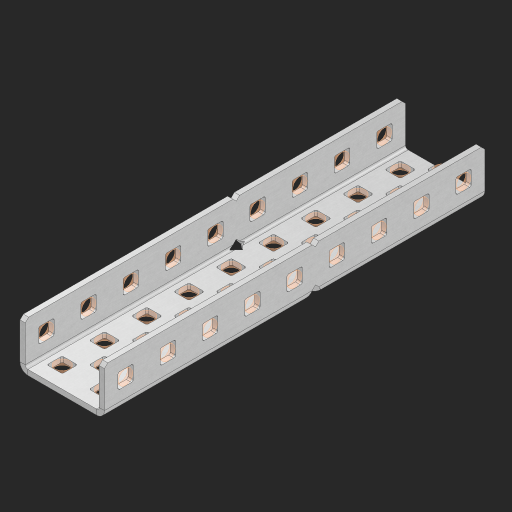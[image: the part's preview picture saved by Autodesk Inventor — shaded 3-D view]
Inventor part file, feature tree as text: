
AUTODESK INVENTOR PART (.ipt)
format: ipt  version: 2023 (Build 270158000, 158)  size: 888,320 bytes
history: native  units: in
note: dims shown in document units (in); Inventor stores cm internally (conversion verified against a paired STEP export)
features: other x52, extrude x43, sheet_metal_op x11, sketch x10, pattern_linear x2, mirror x1, chamfer x1
ambient origin geometry x8: Origin, YZ Plane, XZ Plane, XY Plane, X Axis, Y Axis, Z Axis, Center Point
bodies: Solid1 (feature_tree), Body (feature_tree)
feature tree (120):
  sheet_metal_op  "Flanges"
  other  "Flange Pattern Plane"
  other  "Flange Pattern Sketch"
  sheet_metal_op  "Flange Pattern"
  sheet_metal_op  "Body Pattern"
  pattern_linear  "Center Pattern"  Spacing1=0.0625in  [1 undecoded]
  other  "Arc Length"
  mirror  "Notch Mirror"
  pattern_linear  "Notch Pattern"  Spacing1=0.182in  [1 undecoded]
  chamfer  "End Chamfer"
  extrude  "Half Cut"  Depth=0.02in
  sketch  "Sketch1"  dims[d0=1.0in]
  other  "Plate1"
  sketch  "Sketch2"  dims[d1=4.5in]
  other  "Plate2"
  sheet_metal_op  "Bend1"
  sheet_metal_op  "Corner1"
  sketch  "Sketch3"  dims[d2=0.0625in]
  sketch  "Sketch7"  dims[d3=0.0625in]
  other  "Srf1"
  other  "Srf2"
  sketch  "Sketch8"  dims[d4=0.0312in]
  sketch  "Sketch9"  dims[d5=0.125in]
  other  "Srf91"
  sheet_metal_op  "Body Pattern Sketch"
  other  "Srf92"
  sketch  "Sketch13"  dims[d6=0.0625in]
  sketch  "Sketch14"  dims[d7=0.5in d8=90.0deg d9=0.0312in]
  sketch  "Sketch15"  dims[d10=0.25in]
  sketch  "Sketch16"  dims[d11=0.0625in d12=0.0625in d16=0.182in d17=0.02in d18=0.0625in d19=0.0in d20=0.25in d21=0.25in d38=3.5433in d40=0.5in d41=0.7874in d43=1.0in d46=0.172in d47=1.0in d48=0.0in d49=0.182in d50=0.02in d51=0.25in d52=0.25in d53=0.0625in d54=0.0in d55=0.172in d56=1.0in d57=0.0in d58=0.25in d60=3.5433in d62=0.5in d63=0.7874in d65=0.5in d85=0.1473in d86=0.1782in d88=0.04in d89=0.0625in d90=0.0in d91=0.04in d92=0.0491in d95=2.5in d96=0.04in d97=0.25in d98=45.0deg d99=0.25in d100=0.5in d101=0.0in d102=2.497in d106=0.182in d107=0.02in d108=0.5in d109=0.5in d110=0.0625in d111=0.0in d112=0.172in d113=0.5in d114=0.0in d117=0.5in d118=0.5in d119=0.5in]
  other  "Srf786"
  other  "Srf823"
  other  "Srf824"
  other  "Srf825"
  other  "Srf826"
  other  "Srf827"
  other  "Srf828"
  other  "Srf829"
  other  "Srf856"
  other  "Srf857"
  other  "Srf858"
  other  "Srf859"
  other  "Srf860"
  other  "Srf861"
  other  "Srf862"
  other  "Srf889"
  other  "Srf890"
  other  "Srf891"
  other  "Srf892"
  other  "Srf893"
  other  "Srf894"
  other  "Srf895"
  other  "Srf896"
  other  "Srf922"
  other  "Srf923"
  other  "Srf924"
  other  "Srf925"
  other  "Srf926"
  other  "Srf959"
  other  "Srf960"
  other  "Srf961"
  other  "Srf962"
  other  "Srf963"
  other  "Srf1143"
  other  "Srf1144"
  other  "Srf1145"
  other  "Srf1146"
  other  "Srf1199"
  other  "Srf1200"
  other  "Srf1201"
  other  "Srf1202"
  sheet_metal_op  "Flange Stamp"
  sheet_metal_op  "Flange Circle"
  sheet_metal_op  "Body Stamp"
  sheet_metal_op  "Body Circle"
  other  "Center Stamp"
  other  "Center Circle"
  sheet_metal_op  "Notch"
  extrude  "ExtrusionSrf2"  Depth=0.0625in
  extrude  "ExtrusionSrf92"  TaperAngle=0.0deg  [1 undecoded]
  extrude  "ExtrusionSrf823"  Depth=0.5in
  extrude  "ExtrusionSrf824"  Depth=0.5in
  extrude  "ExtrusionSrf825"  Depth=0.5in
  extrude  "ExtrusionSrf826"  Depth=0.5in
  extrude  "ExtrusionSrf827"  Depth=1.0in TaperAngle=0.0deg
  extrude  "ExtrusionSrf828"  Depth=0.5in
  extrude  "ExtrusionSrf829"  Depth=0.02in
  extrude  "ExtrusionSrf856"  Depth=0.5in
  extrude  "ExtrusionSrf857"  Depth=0.5in
  extrude  "ExtrusionSrf858"  Depth=0.0625in
  extrude  "ExtrusionSrf859"  TaperAngle=0.0deg  [1 undecoded]
  extrude  "ExtrusionSrf860"  Depth=0.5in
  extrude  "ExtrusionSrf861"  Depth=1.0in TaperAngle=0.0deg
  extrude  "ExtrusionSrf862"  Depth=0.5in
  extrude  "ExtrusionSrf889"  Depth=0.5in
  extrude  "ExtrusionSrf890"  Depth=0.5in
  extrude  "ExtrusionSrf891"  Depth=0.5in
  extrude  "ExtrusionSrf892"  Depth=0.5in
  extrude  "ExtrusionSrf893"  Depth=0.5in
  extrude  "ExtrusionSrf894"  Depth=0.0625in
  extrude  "ExtrusionSrf895"  TaperAngle=0.0deg  [1 undecoded]
  extrude  "ExtrusionSrf896"  Depth=0.5in
  extrude  "ExtrusionSrf922"  Depth=0.5in
  extrude  "ExtrusionSrf923"  Depth=2.5in
  extrude  "ExtrusionSrf924"  Depth=0.5in TaperAngle=45.0deg
  extrude  "ExtrusionSrf925"  Depth=0.5in
  extrude  "ExtrusionSrf926"  Depth=0.5in TaperAngle=0.0deg
  extrude  "ExtrusionSrf959"  Depth=0.5in
  extrude  "ExtrusionSrf960"  Depth=0.5in
  extrude  "ExtrusionSrf961"  Depth=0.02in
  extrude  "ExtrusionSrf962"  Depth=0.5in
  extrude  "ExtrusionSrf963"  Depth=0.5in
  extrude  "ExtrusionSrf1143"  Depth=0.0625in
  extrude  "ExtrusionSrf1144"  TaperAngle=0.0deg  [1 undecoded]
  extrude  "ExtrusionSrf1145"  Depth=0.5in
  extrude  "ExtrusionSrf1146"  Depth=0.5in TaperAngle=0.0deg
  extrude  "ExtrusionSrf1199"  Depth=0.5in
  extrude  "ExtrusionSrf1200"  Depth=0.5in
  extrude  "ExtrusionSrf1201"  Depth=0.5in
  extrude  "ExtrusionSrf1202"  [1 undecoded]
note: 7 required parameter values undecoded (feature->parameter linkage not recoverable at this tier; creation-order binding heuristic only, values carry confidence <= 0.55)
